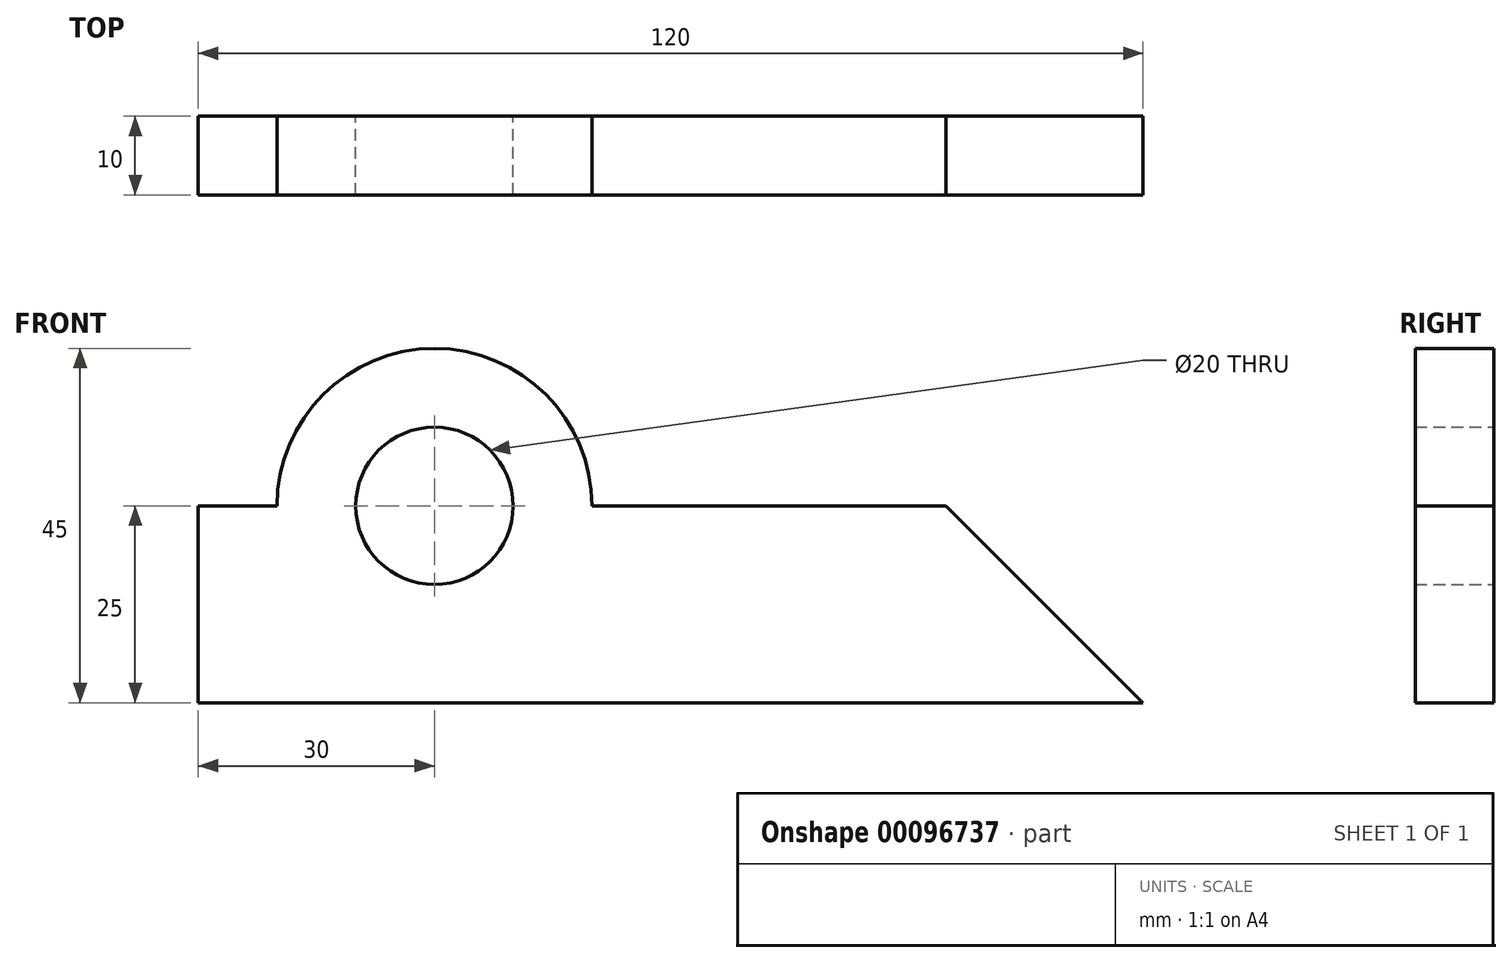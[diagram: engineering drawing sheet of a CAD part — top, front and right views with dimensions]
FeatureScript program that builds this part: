
annotation { "Feature Type Name" : "Feature", "Feature Type Description" : "" }
export const myFeature = defineFeature(function(context is Context, id is Id, definition is map)
    precondition{}
    {
        {
            var Q0;
            Q0=qCreatedBy(makeId("Front.planeOp"),FACE);
            var sketch = newSketch(context, id + "F0", { "sketchPlane" : qUnion([Q0])});
            skLineSegment(sketch, "E0", {"start": v(0, 0) * mm, "end": v(120, 0) * mm});
            skLineSegment(sketch, "E1", {"start": v(120, 0) * mm, "end": v(95, 25) * mm});
            skLineSegment(sketch, "E2", {"start": v(95, 25) * mm, "end": v(50, 25) * mm});
            skLineSegment(sketch, "E3", {"start": v(0, 0) * mm, "end": v(0, 25) * mm});
            skLineSegment(sketch, "E4", {"start": v(0, 25) * mm, "end": v(10, 25) * mm});
            skArc(sketch, "E5", {"start": v(50, 25) * mm, "mid": v(29.9, 45) * mm, "end": v(10, 24.8) * mm});
            skCircle(sketch, "E6", {"center": v(30, 25) * mm, "radius": 10 * mm});
            skSolve(sketch);
        }
        {
            var Q0;
            Q0 = qSketchRegion(id + "F0", true);
            extrude(context, id + "F1", {"entities" : qUnion([Q0]), "depth" : 10 * mm});
        }
    });
